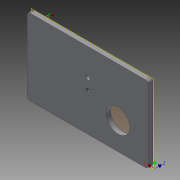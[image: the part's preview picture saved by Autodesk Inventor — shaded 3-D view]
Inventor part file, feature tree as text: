
AUTODESK INVENTOR PART (.ipt)
format: ipt  version: 2015 SP1 (Build 190203100, 203)  size: 2,542,592 bytes
history: native  units: in
note: dims shown in document units (in); Inventor stores cm internally (conversion verified against a paired STEP export)
features: sketch x4, extrude x4, hole x2, plane x1, fillet x1, reference x1
ambient origin geometry x8: Origin, YZ Plane, XZ Plane, XY Plane, X Axis, Y Axis, Z Axis, Center Point
bodies: Solid1 (feature_tree)
feature tree (13):
  plane  "Work Plane1"
  sketch  "Sketch1"  dims[d2=4.2323in d3=2.6575in d4=0.315in d5=0.0in]
  extrude  "Extrusion1"  Depth=0.315in
  fillet  "Fillet1"  Radius=0.315in
  extrude  "Extrusion2"  Depth=0.1181in TaperAngle=0.0deg
  extrude  "Extrusion3"  Depth=0.1181in TaperAngle=0.0deg
  hole  "Hole1"  [1 undecoded]
  extrude  "Extrusion4"  Depth=0.315in
  hole  "Hole2"  [1 undecoded]
  reference  "Reference1"
  sketch  "Sketch2"  dims[d6=0.1969in d7=0.1181in d8=0.0in]
  sketch  "Sketch3"  dims[d9=2.6575in d10=4.2323in]
  sketch  "Sketch4"  dims[d11=0.2617in d12=0.6299in d13=0.1575in d14=0.0787in d15=90.0deg d16=0.874in d17=0.8108in d18=0.1181in d19=0.0in d20=2.9134in d21=1.1811in d22=1.1811in d23=0.5906in d24=1.5748in d25=1.5748in d26=0.1969in d27=1.6535in d28=0.3937in d29=0.0in d30=4.2323in d31=3.4449in d32=0.315in d33=0.2362in d34=0.1575in d35=0.0787in d36=90.0deg d37=0.315in d38=0.8108in]
note: 2 required parameter values undecoded (feature->parameter linkage not recoverable at this tier; creation-order binding heuristic only, values carry confidence <= 0.55)
